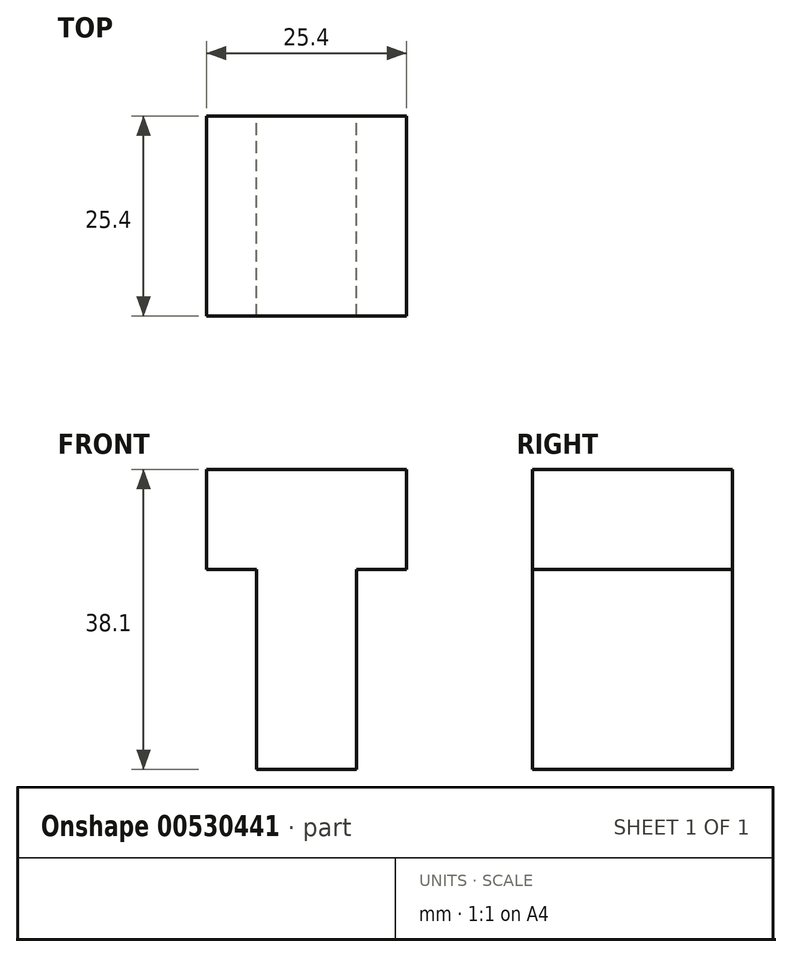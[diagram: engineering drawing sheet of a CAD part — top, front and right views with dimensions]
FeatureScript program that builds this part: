
annotation { "Feature Type Name" : "Feature", "Feature Type Description" : "" }
export const myFeature = defineFeature(function(context is Context, id is Id, definition is map)
    precondition{}
    {
        {
            var Q0;
            Q0=qCreatedBy(makeId("Front.planeOp"),FACE);
            var sketch = newSketch(context, id + "F0", { "sketchPlane" : qUnion([Q0])});
            skLineSegment(sketch, "E0", {"start": v(-46.22, 51.04) * mm, "end": v(-46.22, 38.34) * mm});
            skLineSegment(sketch, "E1", {"start": v(-46.22, 38.34) * mm, "end": v(-39.87, 38.34) * mm});
            skLineSegment(sketch, "E2", {"start": v(-39.87, 38.34) * mm, "end": v(-39.87, 12.94) * mm});
            skLineSegment(sketch, "E3", {"start": v(-39.87, 12.94) * mm, "end": v(-27.17, 12.94) * mm});
            skLineSegment(sketch, "E4", {"start": v(-27.17, 12.94) * mm, "end": v(-27.17, 38.34) * mm});
            skLineSegment(sketch, "E5", {"start": v(-27.17, 38.34) * mm, "end": v(-20.82, 38.34) * mm});
            skLineSegment(sketch, "E6", {"start": v(-20.82, 38.34) * mm, "end": v(-20.82, 51.04) * mm});
            skLineSegment(sketch, "E7", {"start": v(-20.82, 51.04) * mm, "end": v(-46.22, 51.04) * mm});
            skSolve(sketch);
        }
        {
            var Q0;
            Q0=makeQuery(id+"F0.imprint","IMPRINT",FACE,{"disambiguationData":[TD([[makeQuery(id+"F0.imprint","IMPRINT",EDGE,{"derivedFrom":sQuery(id+"F0.wireOp",EDGE,"E0")}),1.0]])]});
            extrude(context, id + "F1", {"entities" : qUnion([Q0]), "depth" : 25.4 * mm, "offsetDistance" : 25.4 * mm});
        }
    });
